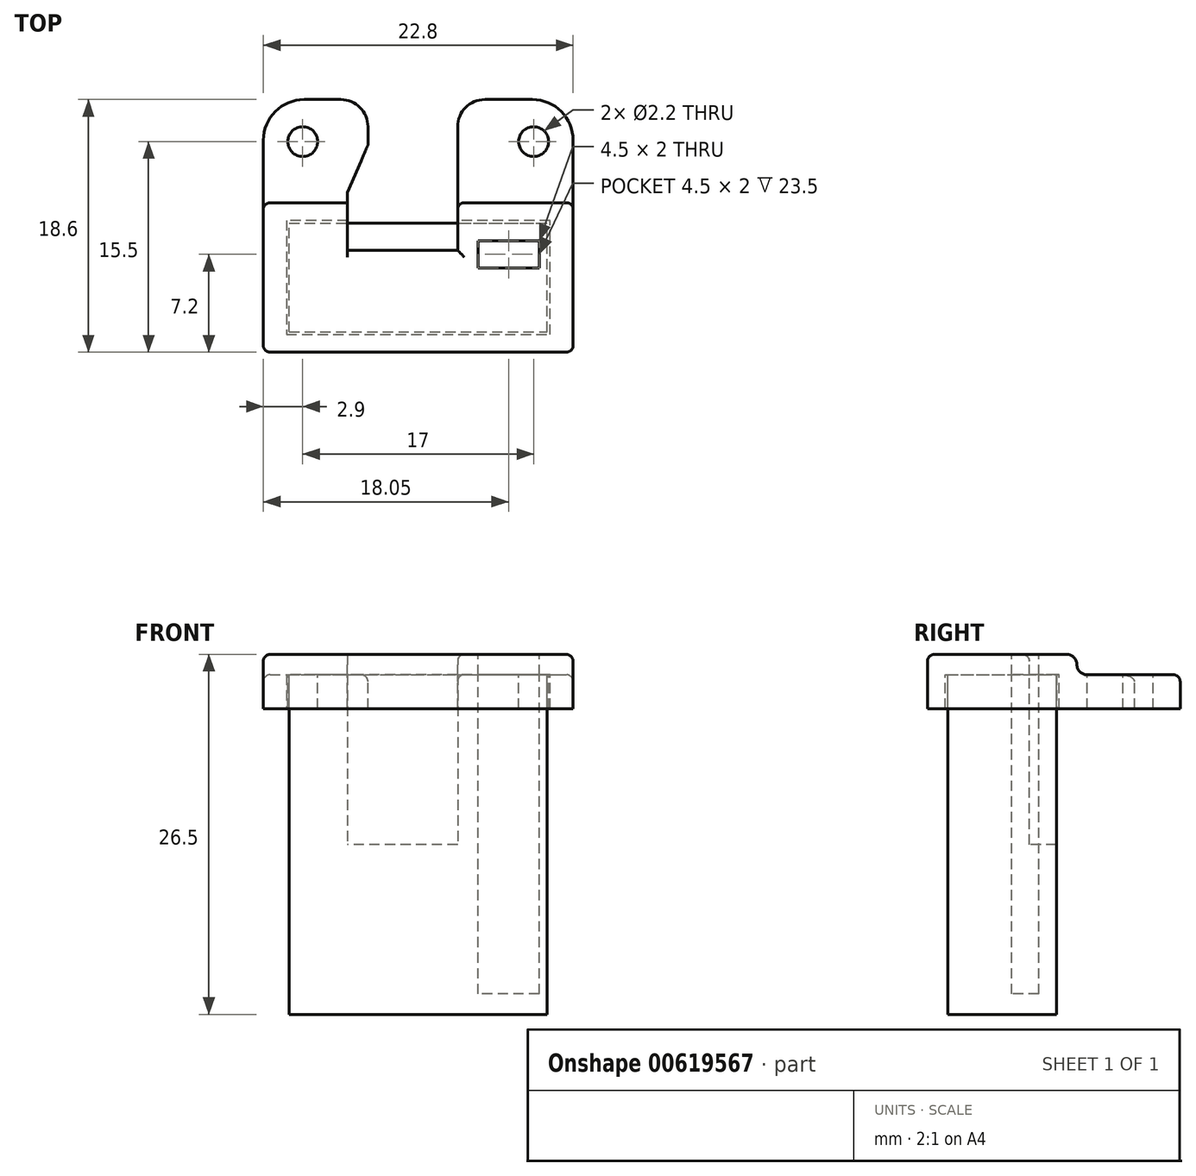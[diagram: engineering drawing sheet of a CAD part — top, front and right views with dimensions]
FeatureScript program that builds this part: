
annotation { "Feature Type Name" : "Feature", "Feature Type Description" : "" }
export const myFeature = defineFeature(function(context is Context, id is Id, definition is map)
    precondition{}
    {
        {
            var Q0;
            Q0=qCreatedBy(makeId("Top.planeOp"),FACE);
            var sketch = newSketch(context, id + "F0", { "sketchPlane" : qUnion([Q0])});
            skLineSegment(sketch, "E0.bottom", {"start": v(-9.5, 0) * mm, "end": v(9.5, 0) * mm});
            skLineSegment(sketch, "E0.top", {"start": v(-9.5, 8) * mm, "end": v(9.5, 8) * mm});
            skLineSegment(sketch, "E0.left", {"start": v(-9.5, 0) * mm, "end": v(-9.5, 8) * mm});
            skLineSegment(sketch, "E0.right", {"start": v(9.5, 0) * mm, "end": v(9.5, 8) * mm});
            skSolve(sketch);
        }
        {
            var Q0;
            Q0 = qSketchRegion(id + "F0", true);
            extrude(context, id + "F1", {"entities" : qUnion([Q0]), "oppositeDirection" : true, "depth" : 25 * mm, "offsetDistance" : 25 * mm});
        }
        {
            var Q0;
            Q0=qCreatedBy(makeId("Top.planeOp"),FACE);
            var sketch = newSketch(context, id + "F2", { "sketchPlane" : qUnion([Q0])});
            skLineSegment(sketch, "E1.bottom", {"start": v(-11.4, 9.5) * mm, "end": v(11.4, 9.5) * mm});
            skLineSegment(sketch, "E1.top", {"start": v(-11.4, -1.5) * mm, "end": v(11.4, -1.5) * mm});
            skLineSegment(sketch, "E1.left", {"start": v(-11.4, 9.5) * mm, "end": v(-11.4, -1.5) * mm});
            skLineSegment(sketch, "E1.right", {"start": v(11.4, 9.5) * mm, "end": v(11.4, -1.5) * mm});
            skSolve(sketch);
        }
        {
            var Q0;
            Q0=makeQuery(id+"F2.imprint","IMPRINT",FACE,{"disambiguationData":[TD([[makeQuery(id+"F2.imprint","IMPRINT",EDGE,{"derivedFrom":sQuery(id+"F2.wireOp",EDGE,"E1.bottom")}),-1.0]])]});
            extrude(context, id + "F3", {"entities" : qUnion([Q0]), "depth" : 1.5 * mm, "offsetDistance" : 25 * mm});
        }
        {
            var Q0;
            Q0=makeQuery(id+"F3.opExtrude","CAP_FACE",FACE,{"disambiguationData":[OSD([sQuery(id+"F2.wireOp",EDGE,"E1.bottom"),sQuery(id+"F2.wireOp",EDGE,"E1.top"),sQuery(id+"F2.wireOp",EDGE,"E1.left"),sQuery(id+"F2.wireOp",EDGE,"E1.right")])],"isStart":true});
            var sketch = newSketch(context, id + "F4", { "sketchPlane" : qUnion([Q0])});
            skLineSegment(sketch, "E2", {"start": v(11.4, -9.5) * mm, "end": v(11.4, 1.5) * mm});
            skLineSegment(sketch, "E3", {"start": v(11.4, 1.5) * mm, "end": v(-11.4, 1.5) * mm});
            skLineSegment(sketch, "E4", {"start": v(-11.4, 1.5) * mm, "end": v(-11.4, -9.5) * mm});
            skLineSegment(sketch, "E5", {"start": v(-11.4, -9.5) * mm, "end": v(-9.7, -9.5) * mm});
            skLineSegment(sketch, "E6", {"start": v(-9.7, 0.2) * mm, "end": v(9.7, 0.2) * mm});
            skLineSegment(sketch, "E7", {"start": v(9.7, 0.2) * mm, "end": v(9.7, -9.5) * mm});
            skLineSegment(sketch, "E8", {"start": v(9.7, -9.5) * mm, "end": v(11.4, -9.5) * mm});
            skLineSegment(sketch, "E9", {"start": v(-9.7, -9.5) * mm, "end": v(-9.7, 0.2) * mm});
            skSolve(sketch);
        }
        {
            var Q0;
            Q0 = qSketchRegion(id + "F4", true);
            extrude(context, id + "F5", {"entities" : qUnion([Q0]), "operationType" : NewBodyOperationType.ADD, "depth" : 2.5 * mm, "offsetDistance" : 25 * mm});
        }
        {
            var Q0;
            Q0=makeQuery(id+"F3.opExtrude","CAP_FACE",FACE,{"disambiguationData":[OSD([sQuery(id+"F2.wireOp",EDGE,"E1.bottom"),sQuery(id+"F2.wireOp",EDGE,"E1.top"),sQuery(id+"F2.wireOp",EDGE,"E1.left"),sQuery(id+"F2.wireOp",EDGE,"E1.right")])],"isStart":true});
            var sketch = newSketch(context, id + "F6", { "sketchPlane" : qUnion([Q0])});
            skLineSegment(sketch, "E10.bottom", {"start": v(11.4, -8.2) * mm, "end": v(-11.4, -8.2) * mm});
            skLineSegment(sketch, "E10.top", {"start": v(8.4, -17.1) * mm, "end": v(-8.4, -17.1) * mm});
            skLineSegment(sketch, "E10.left", {"start": v(11.4, -8.2) * mm, "end": v(11.4, -14.1) * mm});
            skLineSegment(sketch, "E10.right", {"start": v(-11.4, -8.2) * mm, "end": v(-11.4, -14.1) * mm});
            skCircle(sketch, "E11", {"center": v(8.5, -14) * mm, "radius": 1.1 * mm});
            skCircle(sketch, "E12.MirrorC", {"center": v(-8.5, -14) * mm, "radius": 1.1 * mm});
            skPoint(sketch, "E13.visualSharp", {"position": v(11.4, -17.1) * mm});
            skArc(sketch, "E13.filletArc", {"start": v(8.4, -17.1) * mm, "mid": v(10.52, -16.22) * mm, "end": v(11.4, -14.1) * mm});
            skPoint(sketch, "E14.visualSharp", {"position": v(-11.4, -17.1) * mm});
            skArc(sketch, "E14.filletArc", {"start": v(-11.4, -14.1) * mm, "mid": v(-10.52, -16.22) * mm, "end": v(-8.4, -17.1) * mm});
            skSolve(sketch);
        }
        {
            var Q0;
            Q0 = qSketchRegion(id + "F6", true);
            extrude(context, id + "F7", {"entities" : qUnion([Q0]), "operationType" : NewBodyOperationType.ADD, "depth" : 2.5 * mm, "offsetDistance" : 25 * mm});
        }
        {
            var Q0;
            Q0=makeQuery(id+"F7.boolean.opBoolean","INTERSECT",EDGE,{"derivedFrom":[makeQuery(id+"F5.boolean.opBoolean","MERGE",FACE,{"derivedFrom":[makeQuery(id+"F3.opExtrude","SWEPT_FACE",FACE,{"disambiguationData":[OSD([sQuery(id+"F2.wireOp",EDGE,"E1.bottom")])]}),makeQuery(id+"F5.opExtrude","SWEPT_FACE",FACE,{"disambiguationData":[OSD([sQuery(id+"F4.wireOp",EDGE,"E5")])]}),makeQuery(id+"F5.opExtrude","SWEPT_FACE",FACE,{"disambiguationData":[OSD([sQuery(id+"F4.wireOp",EDGE,"E8")])]})]}),makeQuery(id+"F7.opExtrude","CAP_FACE",FACE,{"disambiguationData":[OSD([sQuery(id+"F6.wireOp",EDGE,"E10.bottom"),sQuery(id+"F6.wireOp",EDGE,"E10.top"),sQuery(id+"F6.wireOp",EDGE,"E10.left"),sQuery(id+"F6.wireOp",EDGE,"E10.right"),sQuery(id+"F6.wireOp",EDGE,"E11"),sQuery(id+"F6.wireOp",EDGE,"E12.MirrorC"),sQuery(id+"F6.wireOp",EDGE,"E13.filletArc"),sQuery(id+"F6.wireOp",EDGE,"E14.filletArc")])],"isStart":true})]});
            var Q1;
            Q1=makeQuery(id+"F3.opExtrude","CAP_EDGE",EDGE,{"disambiguationData":[OSD([sQuery(id+"F2.wireOp",EDGE,"E1.bottom")])],"isStart":false});
            fillet(context, id + "F8", {"entities" : qUnion([Q0, Q1]), "radius" : 0.75 * mm, "tangentPropagation" : true, "allowEdgeOverflow" : false});
        }
        {
            var Q0;
            Q0=qCreatedBy(makeId("Top.planeOp"),FACE);
            var sketch = newSketch(context, id + "F9", { "sketchPlane" : qUnion([Q0])});
            skLineSegment(sketch, "E15.bottom", {"start": v(2.9, 23.41) * mm, "end": v(-5.2, 23.41) * mm});
            skLineSegment(sketch, "E15.top", {"start": v(2.9, 6) * mm, "end": v(-5.2, 6) * mm});
            skLineSegment(sketch, "E15.left", {"start": v(2.9, 23.41) * mm, "end": v(2.9, 6) * mm});
            skLineSegment(sketch, "E15.right", {"start": v(-5.2, 23.41) * mm, "end": v(-5.2, 6) * mm});
            skLineSegment(sketch, "E16", {"start": v(-5.2, 10.25) * mm, "end": v(-3.7, 13.75) * mm});
            skLineSegment(sketch, "E17", {"start": v(-3.7, 13.75) * mm, "end": v(-3.7, 23.41) * mm});
            skSolve(sketch);
        }
        {
            var Q0;
            {var subQ1=sQuery(id+"F9.wireOp",EDGE,"E15.top");Q0=makeQuery(id+"F9.imprint","IMPRINT",FACE,{"disambiguationData":[TD([[makeQuery(id+"F9.imprint","IMPRINT",EDGE,{"derivedFrom":subQ1}),-1.0]])]});}
            extrude(context, id + "F10", {"entities" : qUnion([Q0]), "operationType" : NewBodyOperationType.REMOVE, "endBound" : BoundingType.SYMMETRIC, "oppositeDirection" : true, "depth" : 25 * mm, "offsetDistance" : 25 * mm});
        }
        {
            var Q0;
            Q0=makeQuery(id+"F10.boolean.opBoolean","INTERSECT",EDGE,{"derivedFrom":[makeQuery(id+"F7.opExtrude","SWEPT_FACE",FACE,{"disambiguationData":[OSD([sQuery(id+"F6.wireOp",EDGE,"E10.top")])]}),makeQuery(id+"F10.opExtrude","SWEPT_FACE",FACE,{"disambiguationData":[OSD([sQuery(id+"F9.wireOp",EDGE,"E17")])]})]});
            var Q1;
            Q1=makeQuery(id+"F10.boolean.opBoolean","INTERSECT",EDGE,{"derivedFrom":[makeQuery(id+"F7.opExtrude","SWEPT_FACE",FACE,{"disambiguationData":[OSD([sQuery(id+"F6.wireOp",EDGE,"E10.top")])]}),makeQuery(id+"F10.opExtrude","SWEPT_FACE",FACE,{"disambiguationData":[OSD([sQuery(id+"F9.wireOp",EDGE,"E15.left")])]})]});
            fillet(context, id + "F11", {"entities" : qUnion([Q0, Q1]), "radius" : 2 * mm, "tangentPropagation" : true, "allowEdgeOverflow" : false});
        }
        {
            var Q0;
            Q0=makeQuery(id+"F3.opExtrude","CAP_FACE",FACE,{"disambiguationData":[OSD([sQuery(id+"F2.wireOp",EDGE,"E1.bottom"),sQuery(id+"F2.wireOp",EDGE,"E1.top"),sQuery(id+"F2.wireOp",EDGE,"E1.left"),sQuery(id+"F2.wireOp",EDGE,"E1.right")])],"isStart":false});
            var sketch = newSketch(context, id + "F12", { "sketchPlane" : qUnion([Q0])});
            skLineSegment(sketch, "E18.bottom", {"start": v(8.9, 6.7) * mm, "end": v(4.4, 6.7) * mm});
            skLineSegment(sketch, "E18.top", {"start": v(8.9, 4.7) * mm, "end": v(4.4, 4.7) * mm});
            skLineSegment(sketch, "E18.left", {"start": v(8.9, 6.7) * mm, "end": v(8.9, 4.7) * mm});
            skLineSegment(sketch, "E18.right", {"start": v(4.4, 6.7) * mm, "end": v(4.4, 4.7) * mm});
            skSolve(sketch);
        }
        {
            var Q0;
            Q0 = qSketchRegion(id + "F12", true);
            extrude(context, id + "F13", {"entities" : qUnion([Q0]), "operationType" : NewBodyOperationType.REMOVE, "oppositeDirection" : true, "depth" : 25 * mm, "offsetDistance" : 25 * mm});
        }
        {
            var Q0;
            Q0=makeQuery(id+"F5.boolean.opBoolean","MERGE",EDGE,{"derivedFrom":[makeQuery(id+"F3.opExtrude","SWEPT_EDGE",EDGE,{"disambiguationData":[OSD([sQuery(id+"F2.wireOp",EDGE,"E1.top"),sQuery(id+"F2.wireOp",EDGE,"E1.right")])]}),makeQuery(id+"F5.opExtrude","SWEPT_EDGE",EDGE,{"disambiguationData":[OSD([sQuery(id+"F4.wireOp",EDGE,"E2"),sQuery(id+"F4.wireOp",EDGE,"E3")])]})]});
            var Q1;
            Q1=makeQuery(id+"F5.boolean.opBoolean","MERGE",EDGE,{"derivedFrom":[makeQuery(id+"F3.opExtrude","SWEPT_EDGE",EDGE,{"disambiguationData":[OSD([sQuery(id+"F2.wireOp",EDGE,"E1.top"),sQuery(id+"F2.wireOp",EDGE,"E1.left")])]}),makeQuery(id+"F5.opExtrude","SWEPT_EDGE",EDGE,{"disambiguationData":[OSD([sQuery(id+"F4.wireOp",EDGE,"E3"),sQuery(id+"F4.wireOp",EDGE,"E4")])]})]});
            fillet(context, id + "F14", {"entities" : qUnion([Q0, Q1]), "radius" : 0.5 * mm, "tangentPropagation" : true, "allowEdgeOverflow" : false});
        }
        {
            var Q0;
            Q0=makeQuery(id+"F3.opExtrude","CAP_EDGE",EDGE,{"disambiguationData":[OSD([sQuery(id+"F2.wireOp",EDGE,"E1.right")])],"isStart":false});
            fillet(context, id + "F15", {"entities" : qUnion([Q0]), "radius" : 0.5 * mm, "tangentPropagation" : true, "allowEdgeOverflow" : false});
        }
        {
            var Q0;
            Q0=makeQuery(id+"F10.boolean.opBoolean","INTERSECT",EDGE,{"derivedFrom":[makeQuery(id+"F3.opExtrude","CAP_FACE",FACE,{"disambiguationData":[OSD([sQuery(id+"F2.wireOp",EDGE,"E1.bottom"),sQuery(id+"F2.wireOp",EDGE,"E1.top"),sQuery(id+"F2.wireOp",EDGE,"E1.left"),sQuery(id+"F2.wireOp",EDGE,"E1.right")])],"isStart":false}),makeQuery(id+"F10.opExtrude","SWEPT_FACE",FACE,{"disambiguationData":[OSD([sQuery(id+"F9.wireOp",EDGE,"E15.top")])]})]});
            fillet(context, id + "F16", {"entities" : qUnion([Q0]), "radius" : 0.5 * mm, "tangentPropagation" : true, "allowEdgeOverflow" : false});
        }
    });
